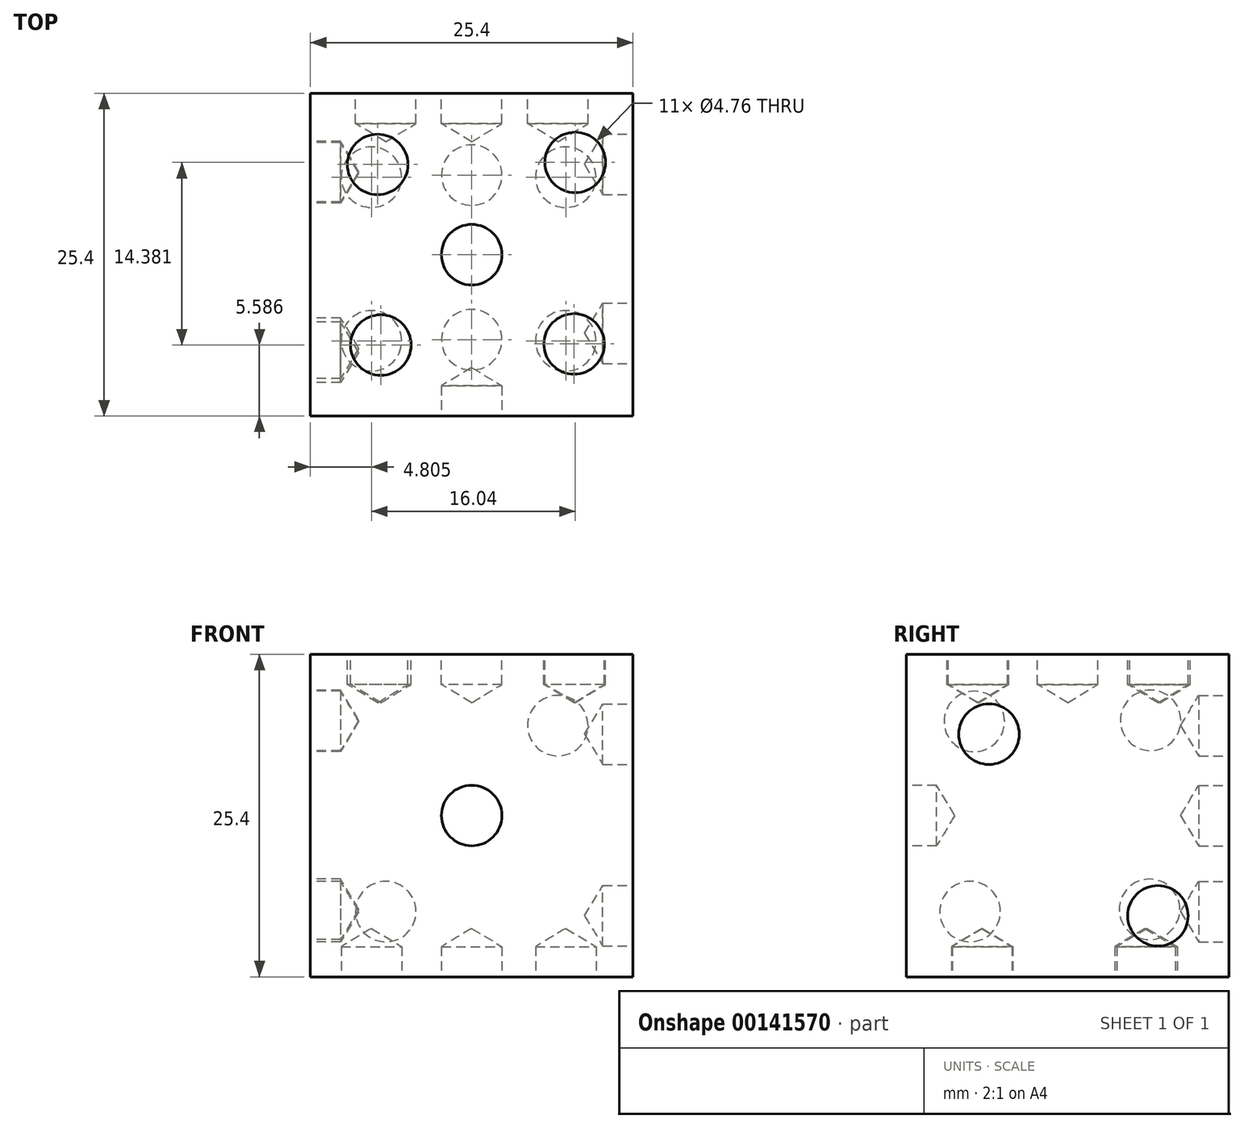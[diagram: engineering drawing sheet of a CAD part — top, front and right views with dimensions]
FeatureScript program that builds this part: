
annotation { "Feature Type Name" : "Feature", "Feature Type Description" : "" }
export const myFeature = defineFeature(function(context is Context, id is Id, definition is map)
    precondition{}
    {
        {
            var Q0;
            Q0=qCreatedBy(makeId("Front.planeOp"),FACE);
            var sketch = newSketch(context, id + "F0", { "sketchPlane" : qUnion([Q0])});
            skLineSegment(sketch, "E0.bottom", {"start": v(12.7, 12.7) * mm, "end": v(-12.7, 12.7) * mm});
            skLineSegment(sketch, "E0.top", {"start": v(12.7, -12.7) * mm, "end": v(-12.7, -12.7) * mm});
            skLineSegment(sketch, "E0.left", {"start": v(12.7, 12.7) * mm, "end": v(12.7, -12.7) * mm});
            skLineSegment(sketch, "E0.right", {"start": v(-12.7, 12.7) * mm, "end": v(-12.7, -12.7) * mm});
            skPoint(sketch, "E0.middle", {"position": v(0, 0) * mm});
            skSolve(sketch);
        }
        {
            var Q0;
            Q0=makeQuery(id+"F0.imprint","IMPRINT",FACE,{"disambiguationData":[TD([[makeQuery(id+"F0.imprint","IMPRINT",EDGE,{"derivedFrom":sQuery(id+"F0.wireOp",EDGE,"E0.bottom")}),1.0]])]});
            extrude(context, id + "F1", {"entities" : qUnion([Q0]), "endBound" : BoundingType.SYMMETRIC, "depth" : 25.4 * mm});
        }
        {
            var Q0;
            Q0=makeQuery(id+"F1.opExtrude","CAP_FACE",FACE,{"disambiguationData":[OSD([sQuery(id+"F0.wireOp",EDGE,"E0.bottom"),sQuery(id+"F0.wireOp",EDGE,"E0.top"),sQuery(id+"F0.wireOp",EDGE,"E0.left"),sQuery(id+"F0.wireOp",EDGE,"E0.right")])],"isStart":false});
            var sketch = newSketch(context, id + "F2", { "sketchPlane" : qUnion([Q0])});
            skPoint(sketch, "E1", {"position": v(0, 0) * mm});
            skSolve(sketch);
        }
        {
            var Q0;
            Q0=sQuery(id+"F2.wireOp",VERTEX,"E1");
            var Q1;
            Q1=makeQuery(id+"F1.opExtrude","SWEPT_BODY",BODY,{"disambiguationData":[OSD([sQuery(id+"F0.wireOp",EDGE,"E0.bottom"),sQuery(id+"F0.wireOp",EDGE,"E0.top"),sQuery(id+"F0.wireOp",EDGE,"E0.left"),sQuery(id+"F0.wireOp",EDGE,"E0.right")])]});
            hole(context, id + "F3", {"style" : HoleStyle.SIMPLE, "endStyle" : HoleEndStyle.BLIND, "holeDiameter" : 4.76 * mm, "holeDepth" : 2.38 * mm, "locations" : qUnion([Q0]), "scope" : qUnion([Q1])});
        }
        {
            var Q0;
            Q0=makeQuery(id+"F1.opExtrude","SWEPT_FACE",FACE,{"disambiguationData":[OSD([sQuery(id+"F0.wireOp",EDGE,"E0.right")])]});
            var sketch = newSketch(context, id + "F4", { "sketchPlane" : qUnion([Q0])});
            skPoint(sketch, "E2", {"position": v(-6.53, 7.49) * mm});
            skPoint(sketch, "E3", {"position": v(7.35, 7.4) * mm});
            skPoint(sketch, "E4", {"position": v(-6.44, -7.4) * mm});
            skPoint(sketch, "E5", {"position": v(7.69, -7.56) * mm});
            skSolve(sketch);
        }
        {
            var Q0;
            Q0=sQuery(id+"F4.wireOp",VERTEX,"E2");
            var Q1;
            Q1=sQuery(id+"F4.wireOp",VERTEX,"E4");
            var Q2;
            Q2=sQuery(id+"F4.wireOp",VERTEX,"E3");
            var Q3;
            Q3=sQuery(id+"F4.wireOp",VERTEX,"E5");
            var Q4;
            Q4=makeQuery(id+"F1.opExtrude","SWEPT_BODY",BODY,{"disambiguationData":[OSD([sQuery(id+"F0.wireOp",EDGE,"E0.bottom"),sQuery(id+"F0.wireOp",EDGE,"E0.top"),sQuery(id+"F0.wireOp",EDGE,"E0.left"),sQuery(id+"F0.wireOp",EDGE,"E0.right")])]});
            hole(context, id + "F5", {"style" : HoleStyle.SIMPLE, "endStyle" : HoleEndStyle.BLIND, "holeDiameter" : 4.76 * mm, "holeDepth" : 2.38 * mm, "locations" : qUnion([Q0, Q1, Q2, Q3]), "scope" : qUnion([Q4])});
        }
        {
            var Q0;
            Q0=makeQuery(id+"F1.opExtrude","CAP_FACE",FACE,{"disambiguationData":[OSD([sQuery(id+"F0.wireOp",EDGE,"E0.bottom"),sQuery(id+"F0.wireOp",EDGE,"E0.top"),sQuery(id+"F0.wireOp",EDGE,"E0.left"),sQuery(id+"F0.wireOp",EDGE,"E0.right")])],"isStart":true});
            var sketch = newSketch(context, id + "F6", { "sketchPlane" : qUnion([Q0])});
            skPoint(sketch, "E6", {"position": v(0, 0) * mm});
            skPoint(sketch, "E7", {"position": v(-6.78, 7.07) * mm});
            skPoint(sketch, "E8", {"position": v(6.77, -7.56) * mm});
            skSolve(sketch);
        }
        {
            var Q0;
            Q0=sQuery(id+"F6.wireOp",VERTEX,"E7");
            var Q1;
            Q1=sQuery(id+"F6.wireOp",VERTEX,"E6");
            var Q2;
            Q2=sQuery(id+"F6.wireOp",VERTEX,"E8");
            var Q3;
            Q3=makeQuery(id+"F1.opExtrude","SWEPT_BODY",BODY,{"disambiguationData":[OSD([sQuery(id+"F0.wireOp",EDGE,"E0.bottom"),sQuery(id+"F0.wireOp",EDGE,"E0.top"),sQuery(id+"F0.wireOp",EDGE,"E0.left"),sQuery(id+"F0.wireOp",EDGE,"E0.right")])]});
            hole(context, id + "F7", {"style" : HoleStyle.SIMPLE, "endStyle" : HoleEndStyle.BLIND, "holeDiameter" : 4.76 * mm, "holeDepth" : 2.38 * mm, "locations" : qUnion([Q0, Q1, Q2]), "scope" : qUnion([Q3])});
        }
        {
            var Q0;
            Q0=makeQuery(id+"F1.opExtrude","SWEPT_FACE",FACE,{"disambiguationData":[OSD([sQuery(id+"F0.wireOp",EDGE,"E0.left")])]});
            var sketch = newSketch(context, id + "F8", { "sketchPlane" : qUnion([Q0])});
            skPoint(sketch, "E9", {"position": v(-6.2, 6.4) * mm});
            skPoint(sketch, "E10", {"position": v(7.1, -7.9) * mm});
            skSolve(sketch);
        }
        {
            var Q0;
            Q0=sQuery(id+"F8.wireOp",VERTEX,"E9");
            var Q1;
            Q1=sQuery(id+"F8.wireOp",VERTEX,"E10");
            var Q2;
            Q2=makeQuery(id+"F1.opExtrude","SWEPT_BODY",BODY,{"disambiguationData":[OSD([sQuery(id+"F0.wireOp",EDGE,"E0.bottom"),sQuery(id+"F0.wireOp",EDGE,"E0.top"),sQuery(id+"F0.wireOp",EDGE,"E0.left"),sQuery(id+"F0.wireOp",EDGE,"E0.right")])]});
            hole(context, id + "F9", {"style" : HoleStyle.SIMPLE, "endStyle" : HoleEndStyle.BLIND, "holeDiameter" : 4.76 * mm, "holeDepth" : 2.38 * mm, "locations" : qUnion([Q0, Q1]), "scope" : qUnion([Q2])});
        }
        {
            var Q0;
            Q0=makeQuery(id+"F1.opExtrude","SWEPT_FACE",FACE,{"disambiguationData":[OSD([sQuery(id+"F0.wireOp",EDGE,"E0.bottom")])]});
            var sketch = newSketch(context, id + "F10", { "sketchPlane" : qUnion([Q0])});
            skPoint(sketch, "E11", {"position": v(0, 0) * mm});
            skPoint(sketch, "E12", {"position": v(-7.4, 7.1) * mm});
            skPoint(sketch, "E13", {"position": v(-7.16, -7.11) * mm});
            skPoint(sketch, "E14", {"position": v(8.06, -7.03) * mm});
            skPoint(sketch, "E15", {"position": v(8.15, 7.27) * mm});
            skSolve(sketch);
        }
        {
            var Q0;
            Q0=sQuery(id+"F10.wireOp",VERTEX,"E13");
            var Q1;
            Q1=sQuery(id+"F10.wireOp",VERTEX,"E11");
            var Q2;
            Q2=sQuery(id+"F10.wireOp",VERTEX,"E15");
            var Q3;
            Q3=sQuery(id+"F10.wireOp",VERTEX,"E12");
            var Q4;
            Q4=sQuery(id+"F10.wireOp",VERTEX,"E14");
            var Q5;
            Q5=makeQuery(id+"F1.opExtrude","SWEPT_BODY",BODY,{"disambiguationData":[OSD([sQuery(id+"F0.wireOp",EDGE,"E0.bottom"),sQuery(id+"F0.wireOp",EDGE,"E0.top"),sQuery(id+"F0.wireOp",EDGE,"E0.left"),sQuery(id+"F0.wireOp",EDGE,"E0.right")])]});
            hole(context, id + "F11", {"style" : HoleStyle.SIMPLE, "endStyle" : HoleEndStyle.BLIND, "holeDiameter" : 4.76 * mm, "holeDepth" : 2.38 * mm, "locations" : qUnion([Q0, Q1, Q2, Q3, Q4]), "scope" : qUnion([Q5])});
        }
        {
            var Q0;
            Q0=makeQuery(id+"F1.opExtrude","SWEPT_FACE",FACE,{"disambiguationData":[OSD([sQuery(id+"F0.wireOp",EDGE,"E0.top")])]});
            var sketch = newSketch(context, id + "F12", { "sketchPlane" : qUnion([Q0])});
            skPoint(sketch, "E16", {"position": v(0, 6.7) * mm});
            skPoint(sketch, "E17", {"position": v(7.4, 6.78) * mm});
            skPoint(sketch, "E18", {"position": v(-7.9, 6.78) * mm});
            skPoint(sketch, "E19", {"position": v(-7.9, -6.1) * mm});
            skPoint(sketch, "E20", {"position": v(0, -6.26) * mm});
            skPoint(sketch, "E21", {"position": v(7.4, -6.1) * mm});
            skSolve(sketch);
        }
        {
            var Q0;
            Q0=sQuery(id+"F12.wireOp",VERTEX,"E17");
            var Q1;
            Q1=sQuery(id+"F12.wireOp",VERTEX,"E21");
            var Q2;
            Q2=sQuery(id+"F12.wireOp",VERTEX,"E20");
            var Q3;
            Q3=sQuery(id+"F12.wireOp",VERTEX,"E16");
            var Q4;
            Q4=sQuery(id+"F12.wireOp",VERTEX,"E18");
            var Q5;
            Q5=sQuery(id+"F12.wireOp",VERTEX,"E19");
            var Q6;
            Q6=makeQuery(id+"F1.opExtrude","SWEPT_BODY",BODY,{"disambiguationData":[OSD([sQuery(id+"F0.wireOp",EDGE,"E0.bottom"),sQuery(id+"F0.wireOp",EDGE,"E0.top"),sQuery(id+"F0.wireOp",EDGE,"E0.left"),sQuery(id+"F0.wireOp",EDGE,"E0.right")])]});
            hole(context, id + "F13", {"style" : HoleStyle.SIMPLE, "endStyle" : HoleEndStyle.BLIND, "holeDiameter" : 4.76 * mm, "holeDepth" : 2.38 * mm, "locations" : qUnion([Q0, Q1, Q2, Q3, Q4, Q5]), "scope" : qUnion([Q6])});
        }
    });
